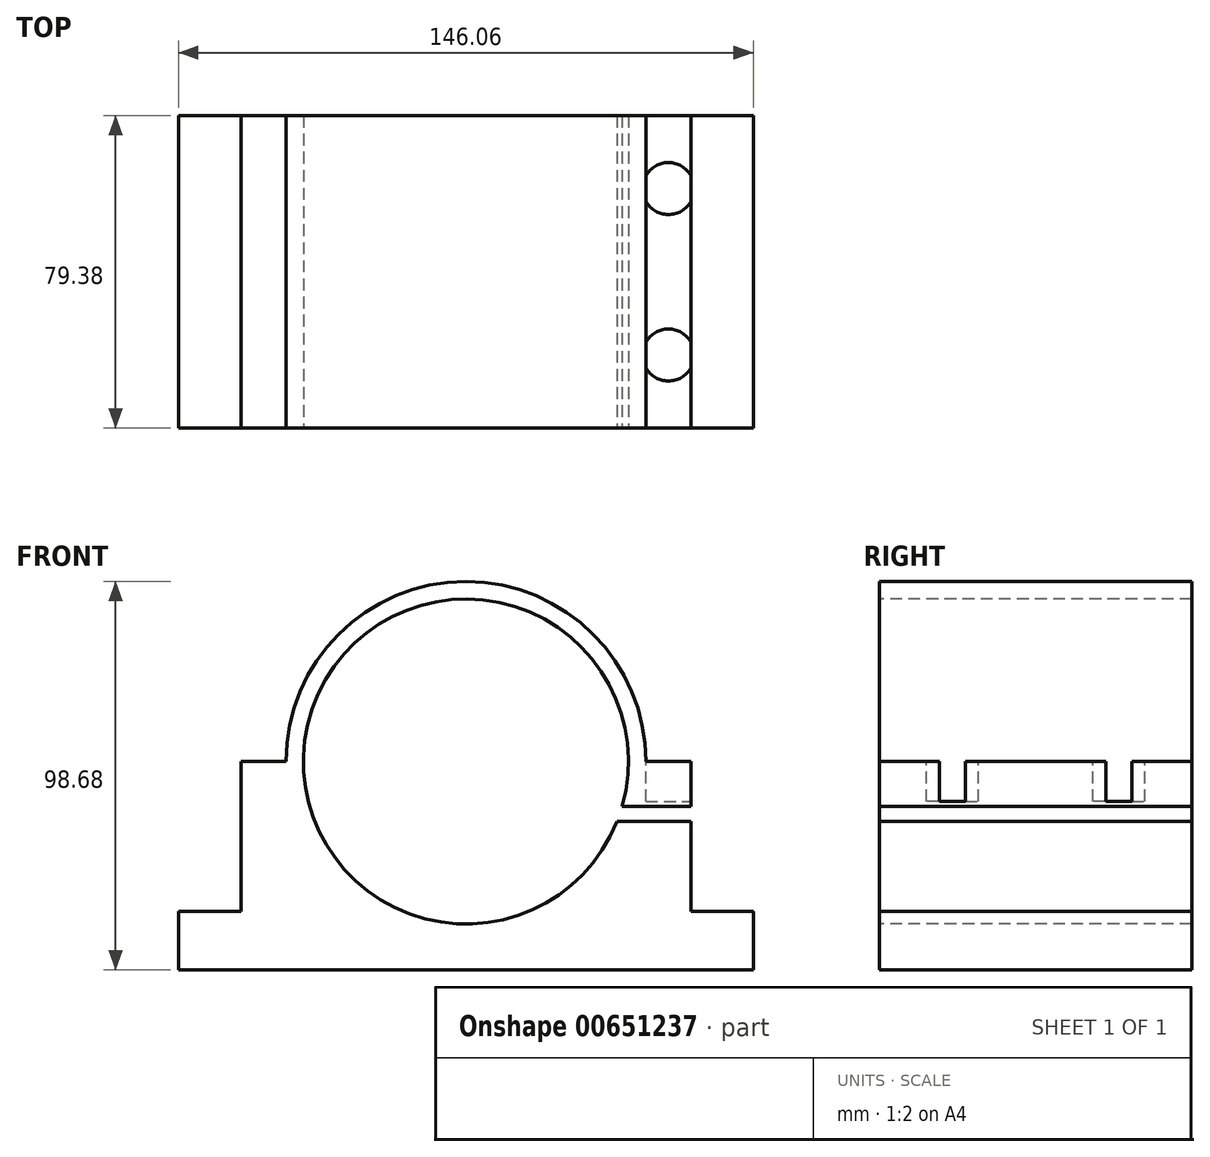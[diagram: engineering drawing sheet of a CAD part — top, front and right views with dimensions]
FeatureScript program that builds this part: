
annotation { "Feature Type Name" : "Feature", "Feature Type Description" : "" }
export const myFeature = defineFeature(function(context is Context, id is Id, definition is map)
    precondition{}
    {
        {
            var Q0;
            Q0=qCreatedBy(makeId("Top.planeOp"),FACE);
            var sketch = newSketch(context, id + "F0", { "sketchPlane" : qUnion([Q0])});
            skLineSegment(sketch, "E0.bottom", {"start": v(-73.03, -39.69) * mm, "end": v(73.03, -39.69) * mm});
            skLineSegment(sketch, "E0.top", {"start": v(-73.03, 39.69) * mm, "end": v(73.03, 39.69) * mm});
            skLineSegment(sketch, "E0.left", {"start": v(-73.03, -39.69) * mm, "end": v(-73.03, 39.69) * mm});
            skLineSegment(sketch, "E0.right", {"start": v(73.03, -39.69) * mm, "end": v(73.03, 39.69) * mm});
            skPoint(sketch, "E0.middle", {"position": v(0, 0) * mm});
            skSolve(sketch);
        }
        {
            var Q0;
            Q0=makeQuery(id+"F0.imprint","IMPRINT",FACE,{"disambiguationData":[TD([[makeQuery(id+"F0.imprint","IMPRINT",EDGE,{"derivedFrom":sQuery(id+"F0.wireOp",EDGE,"E0.bottom")}),1.0]])]});
            extrude(context, id + "F1", {"entities" : qUnion([Q0]), "depth" : 14.86 * mm, "offsetDistance" : 25.4 * mm});
        }
        {
            var Q0;
            Q0=makeQuery(id+"F1.opExtrude","SWEPT_FACE",FACE,{"disambiguationData":[OSD([sQuery(id+"F0.wireOp",EDGE,"E0.bottom")])]});
            var sketch = newSketch(context, id + "F2", { "sketchPlane" : qUnion([Q0])});
            skLineSegment(sketch, "E1", {"start": v(0, 0) * mm, "end": v(0, 52.96) * mm});
            skCircle(sketch, "E2", {"center": v(0, 52.96) * mm, "radius": 41.28 * mm});
            skLineSegment(sketch, "E3", {"start": v(57.15, 52.96) * mm, "end": v(57.15, 14.86) * mm});
            skLineSegment(sketch, "E4", {"start": v(-57.15, 52.96) * mm, "end": v(-57.15, 14.86) * mm});
            skLineSegment(sketch, "E5", {"start": v(-57.15, 52.96) * mm, "end": v(-45.72, 52.96) * mm});
            skLineSegment(sketch, "E6", {"start": v(57.15, 52.96) * mm, "end": v(45.72, 52.96) * mm});
            skArc(sketch, "E7", {"start": v(45.72, 52.96) * mm, "mid": v(0, 98.68) * mm, "end": v(-45.72, 52.96) * mm});
            skSolve(sketch);
        }
        {
            var Q0;
            {var subQ4=sQuery(id+"F2.wireOp",EDGE,"E3");Q0=makeQuery(id+"F2.imprint","IMPRINT",FACE,{"disambiguationData":[TD([[makeQuery(id+"F2.imprint","IMPRINT",EDGE,{"derivedFrom":subQ4}),-1.0]])]});}
            extrude(context, id + "F3", {"entities" : qUnion([Q0]), "operationType" : NewBodyOperationType.ADD, "oppositeDirection" : true, "depth" : 79.38 * mm, "offsetDistance" : 25.4 * mm});
        }
        {
            var Q0;
            {var subQ0=sQuery(id+"F2.wireOp",EDGE,"E2");var subQ1=sQuery(id+"F2.wireOp",EDGE,"E1");var subQ2=makeQuery(id+"F2.imprint","INTERSECT",VERTEX,{"derivedFrom":[subQ1,subQ0]});Q0=makeQuery(id+"F2.imprint","IMPRINT",FACE,{"disambiguationData":[TD([[makeQuery(id+"F2.imprint","IMPRINT",EDGE,{"disambiguationData":[TD([[subQ2,-1.0]])],"derivedFrom":subQ1}),-1.0]])]});}
            var Q1;
            {var subQ0=sQuery(id+"F2.wireOp",EDGE,"E2");var subQ1=sQuery(id+"F2.wireOp",EDGE,"E1");var subQ2=makeQuery(id+"F2.imprint","INTERSECT",VERTEX,{"derivedFrom":[subQ1,subQ0]});Q1=makeQuery(id+"F2.imprint","IMPRINT",FACE,{"disambiguationData":[TD([[makeQuery(id+"F2.imprint","IMPRINT",EDGE,{"disambiguationData":[TD([[subQ2,-1.0]])],"derivedFrom":subQ1}),1.0]])]});}
            extrude(context, id + "F4", {"entities" : qUnion([Q0, Q1]), "operationType" : NewBodyOperationType.REMOVE, "oppositeDirection" : true, "depth" : 85.72 * mm, "offsetDistance" : 25.4 * mm});
        }
        {
            var Q0;
            {var subQ4=sQuery(id+"F2.wireOp",EDGE,"E3");Q0=makeQuery(id+"F2.imprint","IMPRINT",FACE,{"disambiguationData":[TD([[makeQuery(id+"F2.imprint","IMPRINT",EDGE,{"derivedFrom":subQ4}),-1.0]])]});}
            var sketch = newSketch(context, id + "F5", { "sketchPlane" : qUnion([Q0])});
            skLineSegment(sketch, "E8", {"start": v(57.45, 41.54) * mm, "end": v(39.63, 41.54) * mm});
            skLineSegment(sketch, "E9", {"start": v(39.63, 41.54) * mm, "end": v(38.18, 41.54) * mm});
            skLineSegment(sketch, "E10", {"start": v(38.18, 41.54) * mm, "end": v(36.73, 37.74) * mm});
            skLineSegment(sketch, "E11", {"start": v(36.73, 37.74) * mm, "end": v(58.4, 37.74) * mm});
            skLineSegment(sketch, "E12", {"start": v(58.4, 37.74) * mm, "end": v(57.45, 41.54) * mm});
            skSolve(sketch);
        }
        {
            var Q0;
            {var subQ0=sQuery(id+"F5.wireOp",EDGE,"E8");var subQ1=makeQuery(id+"F2.imprint","IMPRINT",EDGE,{"derivedFrom":sQuery(id+"F2.wireOp",EDGE,"E3")});var subQ2=makeQuery(id+"F5.imprint","INTERSECT",VERTEX,{"derivedFrom":[subQ1,subQ0]});Q0=makeQuery(id+"F5.imprint","IMPRINT",FACE,{"disambiguationData":[TD([[makeQuery(id+"F5.imprint","IMPRINT",EDGE,{"disambiguationData":[TD([[subQ2,-1.0]])],"derivedFrom":subQ1}),-1.0]])]});}
            extrude(context, id + "F6", {"entities" : qUnion([Q0]), "operationType" : NewBodyOperationType.REMOVE, "endBound" : BoundingType.THROUGH_ALL, "oppositeDirection" : true, "depth" : 25.4 * mm, "offsetDistance" : 25.4 * mm});
        }
        {
            var Q0;
            Q0=makeQuery(id+"F3.opExtrude","SWEPT_FACE",FACE,{"disambiguationData":[OSD([sQuery(id+"F2.wireOp",EDGE,"E6")])]});
            var sketch = newSketch(context, id + "F7", { "sketchPlane" : qUnion([Q0])});
            skCircle(sketch, "E13", {"center": v(51.44, 21.15) * mm, "radius": 6.6 * mm});
            skCircle(sketch, "E14", {"center": v(51.44, -21.15) * mm, "radius": 6.6 * mm});
            skSolve(sketch);
        }
        {
            var Q0;
            {var subQ0=sQuery(id+"F7.wireOp",EDGE,"E13");var subQ1=sQuery(id+"F2.wireOp",EDGE,"E6");var subQ2=makeQuery(id+"F3.opExtrude","SWEPT_EDGE",EDGE,{"disambiguationData":[OSD([subQ1,sQuery(id+"F2.wireOp",EDGE,"E7")])]});var subQ3=makeQuery(id+"F7.imprint","INTERSECT",VERTEX,{"disambiguationData":[OD(0.0)],"derivedFrom":[subQ2,subQ0]});Q0=makeQuery(id+"F7.imprint","IMPRINT",FACE,{"disambiguationData":[TD([[makeQuery(id+"F7.imprint","IMPRINT",EDGE,{"disambiguationData":[TD([[subQ3,1.0]])],"derivedFrom":subQ0}),1.0]])]});}
            var Q1;
            {var subQ0=sQuery(id+"F7.wireOp",EDGE,"E14");var subQ1=sQuery(id+"F2.wireOp",EDGE,"E6");var subQ2=makeQuery(id+"F3.opExtrude","SWEPT_EDGE",EDGE,{"disambiguationData":[OSD([subQ1,sQuery(id+"F2.wireOp",EDGE,"E7")])]});var subQ3=makeQuery(id+"F7.imprint","INTERSECT",VERTEX,{"disambiguationData":[OD(0.0)],"derivedFrom":[subQ2,subQ0]});Q1=makeQuery(id+"F7.imprint","IMPRINT",FACE,{"disambiguationData":[TD([[makeQuery(id+"F7.imprint","IMPRINT",EDGE,{"disambiguationData":[TD([[subQ3,1.0]])],"derivedFrom":subQ0}),1.0]])]});}
            extrude(context, id + "F8", {"entities" : qUnion([Q0, Q1]), "operationType" : NewBodyOperationType.REMOVE, "oppositeDirection" : true, "depth" : 10.16 * mm, "offsetDistance" : 25.4 * mm});
        }
    });
